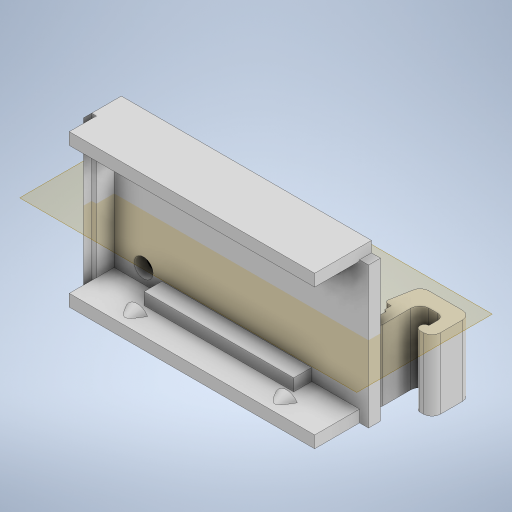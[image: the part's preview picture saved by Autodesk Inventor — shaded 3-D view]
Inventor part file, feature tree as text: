
AUTODESK INVENTOR PART (.ipt)
format: ipt  version: 2023 (Build 270158030, 158C)  size: 885,248 bytes
history: native  units: mm
features: extrude x12, other x8, plane x8, sketch x7, projected_geometry x5, mirror x2, chamfer x1, reference x1
ambient origin geometry x8: Origin, YZ Plane, XZ Plane, XY Plane, X Axis, Y Axis, Z Axis, Center Point
bodies: Body1 (feature_tree), Body2 (feature_tree)
feature tree (44):
  other  "buck-converter-case"
  other  "Blocks"
  sketch  "Sketch1"  dims[d0=2.0mm d1=0.0mm d4=10.0mm d5=0.0mm]
  extrude  "Extrusion1"  Depth=10.0mm TaperAngle=0.0deg
  plane  "Work Plane1"
  extrude  "Extrusion2"  Depth=3.0mm
  extrude  "Extrusion6"  Depth=17.780726mm
  plane  "Work Plane13"
  extrude  "Extrusion16"  Depth=6.409146mm
  plane  "Work Plane14"
  extrude  "Extrusion8"  Depth=1.257608mm
  plane  "Work Plane15"
  mirror  "Mirror4"
  extrude  "Extrusion9"  Depth=0.803745mm
  plane  "Work Plane10"
  extrude  "Extrusion11"  Depth=2.0mm
  plane  "Work Plane16"
  extrude  "Extrusion12"  Depth=2.0mm
  mirror  "Mirror3"
  extrude  "Extrusion13"  TaperAngle=0.0deg  [1 undecoded]
  plane  "Work Plane5"
  extrude  "Extrusion14"  Depth=2.0mm TaperAngle=0.0deg
  extrude  "Extrusion15"  Depth=10.0mm TaperAngle=0.0deg
  chamfer  "Chamfer11"  Distance=1.3mm
  plane  "Work Plane17"
  extrude  "Extrusion17"  Depth=2.0mm
  reference  "Reference1"
  other  "DIN-rail-mount"
  sketch  "Sketch8"  dims[d41=23.55mm d43=3.0mm]
  sketch  "Sketch9"  dims[d44=0.4mm d45=17.780726mm]
  sketch  "Sketch13"  dims[d46=4.630585mm d47=6.409146mm]
  sketch  "Sketch14"  dims[d48=0.917895mm d49=1.257608mm]
  sketch  "Sketch15"  dims[d50=1.6mm d51=0.803745mm]
  other  "board"
  sketch  "Sketch17"  dims[d52=2.954284mm d53=0.7465mm d54=0.5mm d55=0.0mm d56=0.0mm d61=2.0mm d62=0.0mm d65=10.0mm d66=0.0mm d67=1.3mm d76=4.0mm d78=12.0mm d79=-4.537856mm d80=12.0mm d81=0.0mm d82=0.0mm d83=0.0mm d97=21.0mm d98=43.0mm d99=1.3mm d100=0.0mm d101=1.3mm d102=0.0mm d109=2.0mm d110=2.0mm d111=45.0deg d117=3.0mm d123=16.819631mm d124=17.830248mm d125=16.711144mm d126=0.704136mm d127=16.322468mm d129=4.370885mm d130=0.289941mm d131=0.003807mm d132=18.518058mm d133=20.70572mm d137=23.48774mm d138=0.990364mm d150=41.0mm d154=2.0mm d155=0.0mm d158=3.0mm d164=8.0mm d165=8.0mm d167=0.3mm d169=10.0mm d170=0.0mm d171=7.4mm d172=7.8mm d173=1.1mm d174=1.5mm d175=8.0mm d176=8.0mm d178=2.0mm]
  projected_geometry  "Projected Loop16"
  other  "DIN-clip"
  projected_geometry  "Projected Loop17"
  projected_geometry  "Projected Loop18"
  projected_geometry  "Projected Loop19"
  projected_geometry  "Projected Loop20"
  other  "buck-converter-din-rail-mount.iam"
  other  "Power Buck Converter:1"
  other  "DIN-clip:1"
note: 1 required parameter value undecoded (feature->parameter linkage not recoverable at this tier; creation-order binding heuristic only, values carry confidence <= 0.55)
